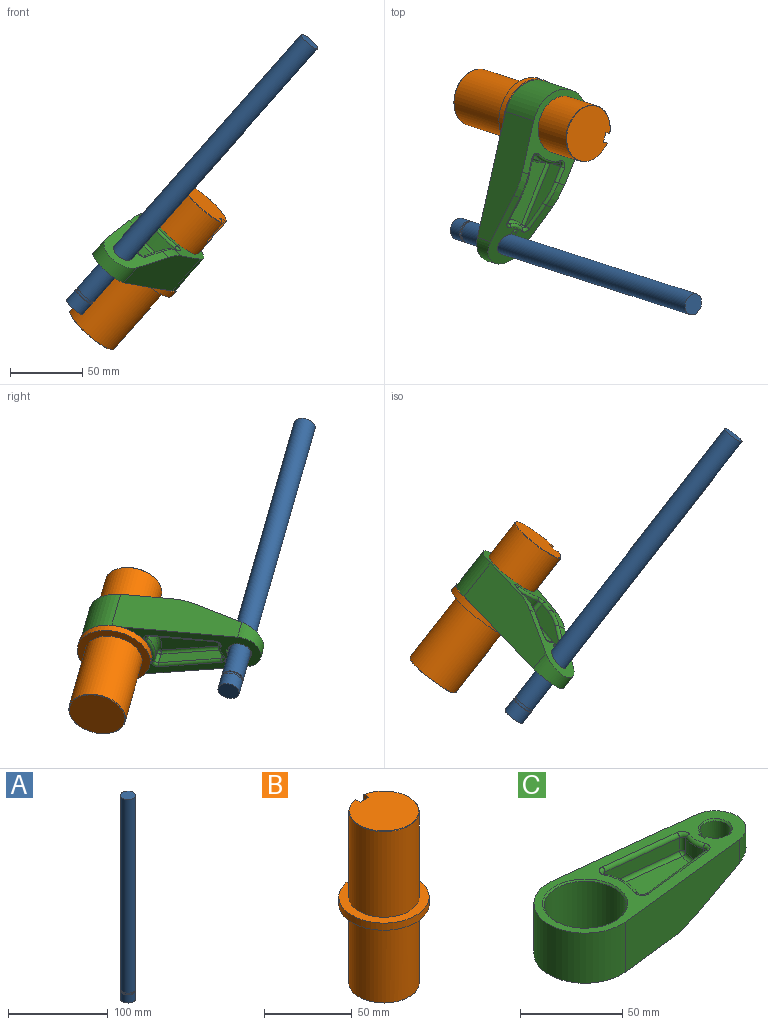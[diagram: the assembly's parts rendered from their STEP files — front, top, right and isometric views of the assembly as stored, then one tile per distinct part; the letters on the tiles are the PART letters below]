
ASSEMBLY  parts=3 mates=2
PART A: 7 faces, bbox 15x15x250 mm
  f0: cylinder r=7.5mm len=238mm, axis (0,0,1), area 11215.5mm2, adj f1,f6
  f1: plane 15x15mm, normal (0,0,1), area 176.7mm2, adj f0
  f2: plane 15x15mm, normal (0,0,-1), area 176.7mm2, adj f3
  f3: cylinder r=7.5mm len=15mm, axis (0,0,1), area 471.2mm2, adj f2,f4
  f4: plane 15x15mm, normal (0,0,1), area 35.7mm2, adj f3,f5
  f5: cylinder r=6.7mm len=13.4mm, axis (0,0,1), area 84.2mm2, adj f4,f6
  f6: plane 15x15mm, normal (0,0,-1), area 35.7mm2, adj f0,f5
PART B: 13 faces, bbox 51.5x51.5x120 mm
  f0: cylinder r=20mm len=59.7mm, axis (0,0,-1), area 7379.4mm2, adj f5,f7,f8,f10,f11
  f1: plane 39.4x39.4mm, normal (0,0,-1), area 1219.2mm2, adj f12
  f2: cylinder r=20mm len=54.7mm, axis (0,0,-1), area 6873.8mm2, adj f3,f12
  f3: plane 51.49x51.49mm, normal (0,0,-1), area 825.8mm2, adj f2,f4
  f4: cylinder r=25.75mm len=51.49mm, axis (0,0,-1), area 808.8mm2, adj f3,f5
  f5: plane 51.49x51.49mm, normal (0,0,1), area 825.8mm2, adj f0,f4
  f6: plane 39.4x39.09mm, normal (0,0,1), area 1191.9mm2, adj f7,f8,f9,f11
  f7: plane 15x4mm, normal (-1,0,0), area 60mm2, adj f0,f6,f9,f10,f11
  f8: plane 15x4mm, normal (1,0,0), area 60mm2, adj f0,f6,f9,f10,f11
  f9: plane 18.5x7mm, normal (0,1,0), area 124.2mm2, adj f6,f7,f8,f10
  f10: cylinder r=3.5mm len=7mm, axis (0,-1,0), area 45.7mm2, adj f0,f7,f8,f9
  f11: cone r=20mm half-angle=45deg, axis (0,0,-1), area 49.9mm2, adj f0,f6,f7,f8
  f12: cone r=19.7mm half-angle=45deg, axis (0,0,1), area 52.9mm2, adj f1,f2
PART C: 79 faces, bbox 130x50x30 mm
  f0: cylinder r=2mm len=0.68mm, axis (0,0,-1), area 0mm2, adj f1,f78
  f1: sphere r=2mm, area 7.5mm2, adj f0,f2,f75,f76,f77
  f2: cylinder r=2mm len=13.6mm, axis (-0.99,0.1,0), area 42.3mm2, adj f1,f3,f73,f74
  f3: cylinder r=2mm len=33.28mm, axis (-0.99,0.11,0), area 104.5mm2, adj f2,f4,f72,f74
  f4: sphere r=2mm, area 8.4mm2, adj f3,f5,f71
  f5: torus R=30mm, axis (0,0,1), area 74.4mm2, adj f4,f6,f70,f74
  f6: sphere r=2mm, area 8.4mm2, adj f5,f7,f69
  f7: cylinder r=2mm len=46.63mm, axis (0.99,0.11,0), area 146.7mm2, adj f6,f8,f68,f74
  f8: sphere r=2mm, area 7.4mm2, adj f7,f9,f66,f67,f77
  f9: cylinder r=2mm len=0.58mm, axis (0,0,-1), area 0mm2, adj f8,f10,f65
  f10: bspline ~5.54x4.46mm, area 18.3mm2, adj f9,f11,f63,f64,f66,f67
  f11: cylinder r=2mm len=19.64mm, axis (0.93,0.1,0.34), area 64.5mm2, adj f10,f12,f63,f68
  f12: bspline ~30.05x6.46mm, area 55mm2, adj f11,f13,f62,f68
  f13: cylinder r=50mm len=17.1mm, axis (0,-1,0), area 104.7mm2, adj f12,f14,f61,f63
  f14: plane 88.92x30.03mm, normal (0.11,-0.99,0), area 2329.6mm2, adj f13,f15,f25,f60,f61,f63
  f15: cylinder r=25mm len=50mm, axis (0,0,-1), area 2523.2mm2, adj f14,f16,f25,f61
  f16: plane 88.92x30.03mm, normal (0.11,0.99,0), area 2329.6mm2, adj f15,f17,f25,f60,f61,f63
  f17: cylinder r=50mm len=17.1mm, axis (0,-1,0), area 104.7mm2, adj f16,f18,f61,f63
  f18: bspline ~30.05x6.46mm, area 55mm2, adj f17,f19,f21,f72
  f19: cylinder r=2mm len=6.28mm, axis (-0.93,0.1,-0.34), area 18.5mm2, adj f18,f20,f63,f72,f73
  f20: cylinder r=2mm len=14.27mm, axis (-0.94,0.1,-0.34), area 46mm2, adj f19,f63,f73,f78
  f21: cylinder r=2mm len=11.48mm, axis (0.99,-0.11,0), area 35.6mm2, adj f18,f22,f61,f72
  f22: torus R=4mm, axis (0,0,1), area 17.9mm2, adj f21,f23,f61,f71
  f23: torus R=26mm, axis (0,0,1), area 70.6mm2, adj f22,f24,f61,f70
  f24: torus R=4mm, axis (0,0,1), area 17.9mm2, adj f23,f61,f62,f69
  f25: plane 130x50mm, normal (0,0,1), area 1976.4mm2, adj f14,f15,f16,f26,f44,f45,f46,f47
  f26: cylinder r=2mm len=46.63mm, axis (0.99,-0.11,0), area 146.7mm2, adj f25,f27,f44,f50
  f27: plane 46.4x8mm, normal (-0.11,-0.99,0), area 373.5mm2, adj f26,f28,f42,f43
  f28: cylinder r=2mm len=46.63mm, axis (-0.99,0.11,0), area 146.7mm2, adj f27,f29,f40,f41
  f29: sphere r=2mm, area 7.4mm2, adj f28,f30,f43
  f30: torus R=17.5mm, axis (0,0,1), area 40.9mm2, adj f29,f31,f39,f41
  f31: sphere r=2mm, area 7.4mm2, adj f30,f32,f38
  f32: cylinder r=2mm len=46.63mm, axis (0.99,0.11,0), area 146.7mm2, adj f31,f33,f37,f41
  f33: sphere r=2mm, area 8.4mm2, adj f32,f34,f36
  f34: torus R=30mm, axis (0,0,1), area 74.4mm2, adj f33,f35,f40,f41
  f35: cylinder r=28mm len=22.44mm, axis (0,0,1), area 184.7mm2, adj f34,f36,f42,f45
  f36: cylinder r=2mm len=8mm, axis (0,0,1), area 33.5mm2, adj f33,f35,f37,f46
  f37: plane 46.4x8mm, normal (-0.11,0.99,0), area 373.5mm2, adj f32,f36,f38,f47
  f38: cylinder r=2mm len=8mm, axis (0,0,1), area 29.8mm2, adj f31,f37,f39,f48
  f39: cylinder r=15.5mm len=12.1mm, axis (0,0,1), area 99.5mm2, adj f30,f38,f43,f49
  f40: sphere r=2mm, area 8.4mm2, adj f28,f34,f42
  f41: plane 46.4x24.04mm, normal (0,0,1), area 821.4mm2, adj f28,f30,f32,f34
  f42: cylinder r=2mm len=8mm, axis (0,0,1), area 33.5mm2, adj f27,f35,f40,f44
  f43: cylinder r=2mm len=8mm, axis (0,0,1), area 29.8mm2, adj f27,f29,f39,f50
  f44: torus R=4mm, axis (0,0,1), area 17.9mm2, adj f25,f26,f42,f45
  f45: torus R=26mm, axis (0,0,1), area 70.6mm2, adj f25,f35,f44,f46
  f46: torus R=4mm, axis (0,0,1), area 17.9mm2, adj f25,f36,f45,f47
  f47: cylinder r=2mm len=46.63mm, axis (-0.99,-0.11,0), area 146.7mm2, adj f25,f37,f46,f48
  f48: torus R=4mm, axis (0,0,1), area 15.9mm2, adj f25,f38,f47,f49
  f49: torus R=13.5mm, axis (0,0,1), area 37.2mm2, adj f25,f39,f48,f50
  f50: torus R=4mm, axis (0,0,1), area 15.9mm2, adj f25,f26,f43,f49
  f51: cone r=20mm half-angle=45deg, axis (0,0,1), area 145mm2, adj f25,f52
  f52: cylinder r=20mm len=40mm, axis (0,0,-1), area 3669.4mm2, adj f51,f61
  f53: plane 18.94x4.38mm, normal (0,1,0), area 43.4mm2, adj f25,f54,f55,f56,f57,f59,f63
  f54: plane 4x2.09mm, normal (0,0,-1), area 8.4mm2, adj f53,f55,f58,f59
  f55: plane 4x1.99mm, normal (1,0,0), area 8mm2, adj f53,f54,f58,f63
  f56: cylinder r=7.5mm len=16.54mm, axis (0,0,-1), area 588.4mm2, adj f53,f57,f58,f63
  f57: cone r=7.5mm half-angle=45deg, axis (0,0,1), area 51.6mm2, adj f25,f53,f56,f58
  f58: plane 18.94x4.38mm, normal (0,-1,0), area 43.4mm2, adj f25,f54,f55,f56,f57,f59,f63
  f59: plane 16.94x4mm, normal (1,0,0), area 67.8mm2, adj f25,f53,f54,f58
  f60: cylinder r=15mm len=29.81mm, axis (0,0,-1), area 481.4mm2, adj f14,f16,f25,f63
  f61: plane 64.18x50mm, normal (0,0,-1), area 1081mm2, adj f13,f14,f15,f16,f17,f21,f22,f23
  f62: cylinder r=2mm len=11.48mm, axis (-0.99,-0.11,0), area 35.6mm2, adj f12,f24,f61,f68
  f63: plane 48.72x37.73mm, normal (0.34,0,-0.94), area 852.1mm2, adj f10,f11,f13,f14,f16,f17,f19,f20
  f64: bspline ~12.27x3.79mm, area 46.4mm2, adj f10,f63,f65,f78
  f65: cylinder r=15.49mm len=12.18mm, axis (0,0,-1), area 4.6mm2, adj f9,f64,f76,f77
  f66: cylinder r=2mm len=0.4mm, axis (0,0,-1), area 0mm2, adj f8,f10
  f67: cylinder r=2mm len=1.79mm, axis (0,0,-1), area 1.3mm2, adj f8,f10,f68
  f68: plane 46.4x11mm, normal (-0.11,0.99,0), area 379mm2, adj f7,f11,f12,f62,f67,f69
  f69: cylinder r=2mm len=11mm, axis (0,0,-1), area 46.1mm2, adj f6,f24,f68,f70
  f70: cylinder r=28mm len=22.44mm, axis (0,0,-1), area 254mm2, adj f5,f23,f69,f71
  f71: cylinder r=2mm len=11mm, axis (0,0,-1), area 46.1mm2, adj f4,f22,f70,f72
  f72: plane 33.05x11mm, normal (-0.11,-0.99,0), area 329.1mm2, adj f3,f18,f19,f21,f71,f73
  f73: plane 13.38x6.15mm, normal (-0.1,-0.99,0), area 50mm2, adj f2,f19,f20,f72,f75
  f74: plane 46.44x24.04mm, normal (0,0,-1), area 822.1mm2, adj f2,f3,f5,f7,f77
  f75: cylinder r=2mm len=1.76mm, axis (0,0,-1), area 1.3mm2, adj f1,f73,f78
  f76: cylinder r=2mm len=0.45mm, axis (0,0,-1), area 0mm2, adj f1,f65,f78
  f77: torus R=17.49mm, axis (0,0,1), area 41.2mm2, adj f1,f8,f65,f74
  f78: bspline ~5.56x4.48mm, area 18.5mm2, adj f0,f20,f63,f64,f75,f76
PLACE A rot(axis=(-0.26,0.36,-0.9),112.8deg) t=(-37.24,-60.52,-25.16)mm
PLACE B rot(axis=(-0.25,0.37,-0.9),110.5deg) t=(-18.95,28.15,-33.8)mm
PLACE C rot(axis=(0.57,-0.77,-0.3),155.4deg) t=(1.76,-31.11,5.91)mm
MATE slider A.f0 <-> C.f56  axis (0.65,-0.21,0.73) through (31.41,-82.74,52.46)mm
MATE revolute C.f51 <-> B.f0  axis (-0.65,0.21,-0.73) through (-2.81,22.92,-15.54)mm
